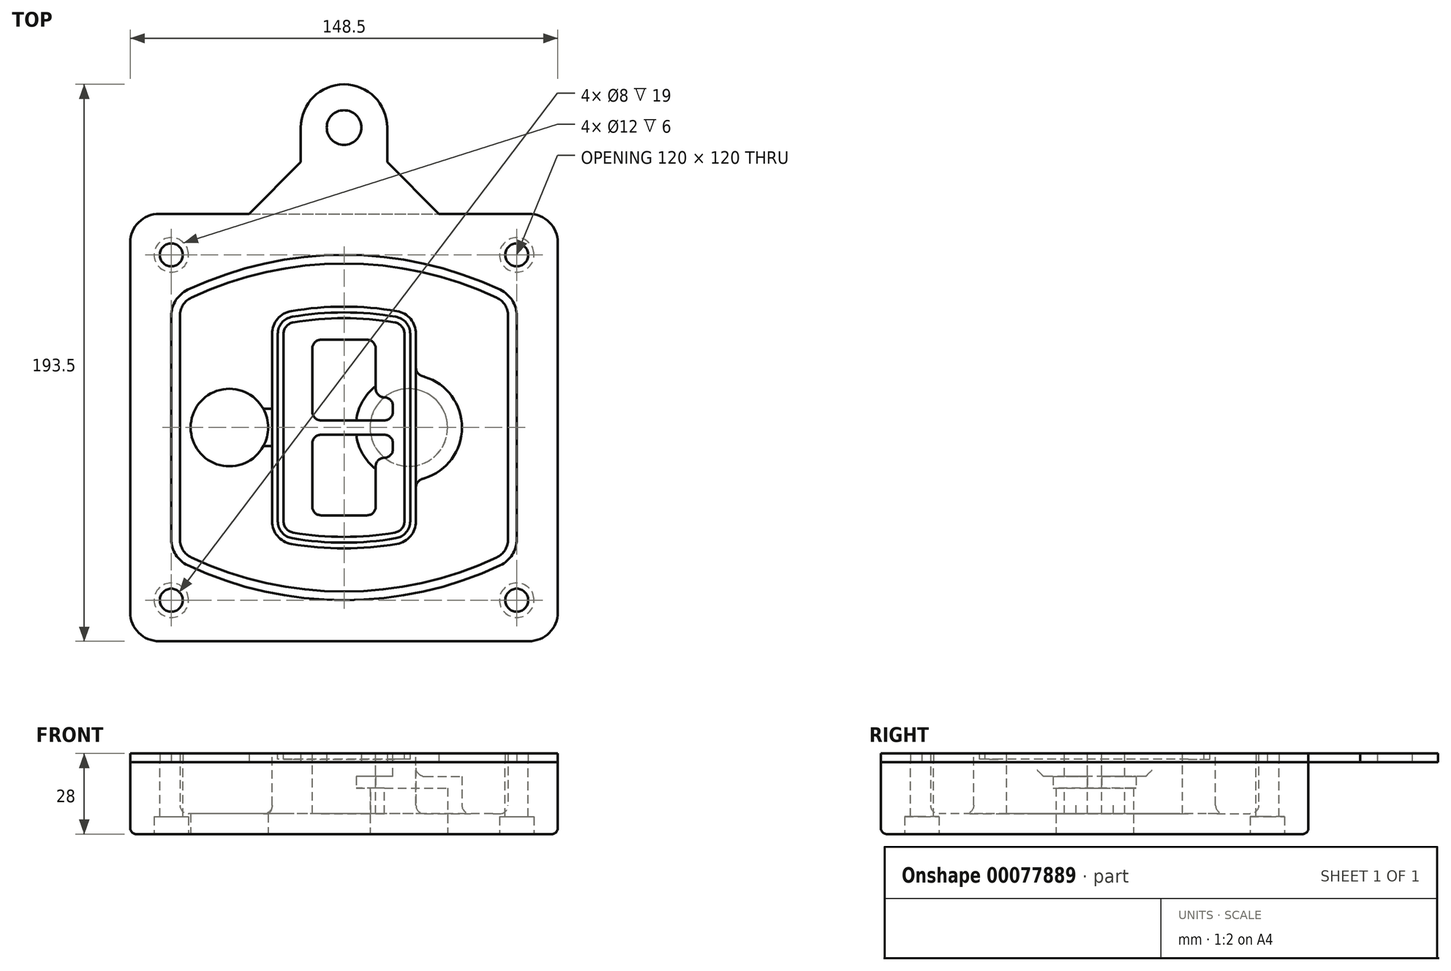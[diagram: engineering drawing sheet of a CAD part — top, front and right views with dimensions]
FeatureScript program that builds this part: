
annotation { "Feature Type Name" : "Feature", "Feature Type Description" : "" }
export const myFeature = defineFeature(function(context is Context, id is Id, definition is map)
    precondition{}
    {
        {
            var Q0;
            Q0=qCreatedBy(makeId("Top.planeOp"),FACE);
            var sketch = newSketch(context, id + "F0", { "sketchPlane" : qUnion([Q0])});
            skPoint(sketch, "E0.rect.middle", {"position": v(0, 0) * mm});
            skLineSegment(sketch, "E1.bottom", {"start": v(-64.25, -74.25) * mm, "end": v(64.25, -74.25) * mm});
            skLineSegment(sketch, "E1.top", {"start": v(-64.25, 74.25) * mm, "end": v(64.25, 74.25) * mm});
            skLineSegment(sketch, "E1.left", {"start": v(-74.25, -64.25) * mm, "end": v(-74.25, 64.25) * mm});
            skLineSegment(sketch, "E1.right", {"start": v(74.25, -64.25) * mm, "end": v(74.25, 64.25) * mm});
            skLineSegment(sketch, "E2", {"start": v(-74.25, 74.25) * mm, "end": v(74.25, -74.25) * mm, "construction": true});
            skLineSegment(sketch, "E3", {"start": v(74.25, 74.25) * mm, "end": v(-74.25, -74.25) * mm, "construction": true});
            skCircle(sketch, "E4", {"center": v(-60, 60) * mm, "radius": 4 * mm});
            skCircle(sketch, "E5", {"center": v(60, 60) * mm, "radius": 4 * mm});
            skCircle(sketch, "E6", {"center": v(60, -60) * mm, "radius": 4 * mm});
            skCircle(sketch, "E7", {"center": v(-60, -60) * mm, "radius": 4 * mm});
            skLineSegment(sketch, "E8", {"start": v(-60, 60) * mm, "end": v(60, 60) * mm, "construction": true});
            skLineSegment(sketch, "E9", {"start": v(60, 60) * mm, "end": v(60, -60) * mm, "construction": true});
            skLineSegment(sketch, "E10", {"start": v(60, -60) * mm, "end": v(-60, -60) * mm, "construction": true});
            skLineSegment(sketch, "E11", {"start": v(-60, -60) * mm, "end": v(-60, 60) * mm, "construction": true});
            skLineSegment(sketch, "E12", {"start": v(-60, 38.83) * mm, "end": v(-60, -38.83) * mm});
            skLineSegment(sketch, "E13", {"start": v(60, 38.83) * mm, "end": v(60, -38.83) * mm});
            skArc(sketch, "E14", {"start": v(54.26, 47.88) * mm, "mid": v(0, 60) * mm, "end": v(-54.26, 47.88) * mm});
            skArc(sketch, "E15", {"start": v(-54.26, -47.88) * mm, "mid": v(0, -60) * mm, "end": v(54.26, -47.88) * mm});
            skLineSegment(sketch, "E16", {"start": v(-60, 0) * mm, "end": v(60, 0) * mm, "construction": true});
            skPoint(sketch, "E17.visualSharp", {"position": v(-60, -45) * mm});
            skArc(sketch, "E17.filletArc", {"start": v(-60, -38.83) * mm, "mid": v(-58.44, -44.2) * mm, "end": v(-54.26, -47.88) * mm});
            skPoint(sketch, "E18.visualSharp", {"position": v(-60, 45) * mm});
            skArc(sketch, "E18.filletArc", {"start": v(-54.26, 47.88) * mm, "mid": v(-58.44, 44.2) * mm, "end": v(-60, 38.83) * mm});
            skPoint(sketch, "E19.visualSharp", {"position": v(60, 45) * mm});
            skArc(sketch, "E19.filletArc", {"start": v(60, 38.83) * mm, "mid": v(58.44, 44.2) * mm, "end": v(54.26, 47.88) * mm});
            skPoint(sketch, "E20.visualSharp", {"position": v(60, -45) * mm});
            skArc(sketch, "E20.filletArc", {"start": v(54.26, -47.88) * mm, "mid": v(58.44, -44.2) * mm, "end": v(60, -38.83) * mm});
            skPoint(sketch, "E21.visualSharp", {"position": v(-74.25, 74.25) * mm});
            skArc(sketch, "E21.filletArc", {"start": v(-64.25, 74.25) * mm, "mid": v(-71.32, 71.32) * mm, "end": v(-74.25, 64.25) * mm});
            skPoint(sketch, "E22.visualSharp", {"position": v(74.25, 74.25) * mm});
            skArc(sketch, "E22.filletArc", {"start": v(74.25, 64.25) * mm, "mid": v(71.32, 71.32) * mm, "end": v(64.25, 74.25) * mm});
            skPoint(sketch, "E23.visualSharp", {"position": v(74.25, -74.25) * mm});
            skArc(sketch, "E23.filletArc", {"start": v(64.25, -74.25) * mm, "mid": v(71.32, -71.32) * mm, "end": v(74.25, -64.25) * mm});
            skPoint(sketch, "E24.visualSharp", {"position": v(-74.25, -74.25) * mm});
            skArc(sketch, "E24.filletArc", {"start": v(-74.25, -64.25) * mm, "mid": v(-71.32, -71.32) * mm, "end": v(-64.25, -74.25) * mm});
            skArc(sketch, "E25.0", {"start": v(57, 38.83) * mm, "mid": v(55.9, 42.58) * mm, "end": v(52.98, 45.17) * mm});
            skLineSegment(sketch, "E25.1", {"start": v(57, 38.83) * mm, "end": v(57, -38.83) * mm});
            skArc(sketch, "E25.2", {"start": v(52.98, -45.17) * mm, "mid": v(55.9, -42.58) * mm, "end": v(57, -38.83) * mm});
            skArc(sketch, "E25.3", {"start": v(-52.98, -45.17) * mm, "mid": v(0, -57) * mm, "end": v(52.98, -45.17) * mm});
            skArc(sketch, "E25.4", {"start": v(-57, -38.83) * mm, "mid": v(-55.9, -42.58) * mm, "end": v(-52.98, -45.17) * mm});
            skArc(sketch, "E25.5", {"start": v(52.98, 45.17) * mm, "mid": v(0, 57) * mm, "end": v(-52.98, 45.17) * mm});
            skLineSegment(sketch, "E25.6", {"start": v(-57, 38.83) * mm, "end": v(-57, -38.83) * mm});
            skArc(sketch, "E25.7", {"start": v(-52.98, 45.17) * mm, "mid": v(-55.9, 42.58) * mm, "end": v(-57, 38.83) * mm});
            skArc(sketch, "E26.0", {"start": v(-55.96, 51.5) * mm, "mid": v(-61.82, 46.33) * mm, "end": v(-64, 38.83) * mm});
            skArc(sketch, "E26.1", {"start": v(55.96, 51.5) * mm, "mid": v(0, 64) * mm, "end": v(-55.96, 51.5) * mm});
            skArc(sketch, "E26.2", {"start": v(64, 38.83) * mm, "mid": v(61.82, 46.33) * mm, "end": v(55.96, 51.5) * mm});
            skLineSegment(sketch, "E26.3", {"start": v(64, 38.83) * mm, "end": v(64, -38.83) * mm});
            skArc(sketch, "E26.4", {"start": v(55.96, -51.5) * mm, "mid": v(61.82, -46.33) * mm, "end": v(64, -38.83) * mm});
            skLineSegment(sketch, "E26.5", {"start": v(-64, 38.83) * mm, "end": v(-64, -38.83) * mm});
            skArc(sketch, "E26.6", {"start": v(-55.96, -51.5) * mm, "mid": v(0, -64) * mm, "end": v(55.96, -51.5) * mm});
            skArc(sketch, "E26.7", {"start": v(-64, -38.83) * mm, "mid": v(-61.82, -46.33) * mm, "end": v(-55.96, -51.5) * mm});
            skSolve(sketch);
        }
        {
            var Q0;
            Q0=makeQuery(id+"F0.imprint","IMPRINT",FACE,{"disambiguationData":[TD([[makeQuery(id+"F0.imprint","IMPRINT",EDGE,{"derivedFrom":sQuery(id+"F0.wireOp",EDGE,"E1.bottom")}),1.0]])]});
            var Q1;
            Q1=makeQuery(id+"F0.imprint","IMPRINT",FACE,{"disambiguationData":[TD([[makeQuery(id+"F0.imprint","IMPRINT",EDGE,{"derivedFrom":sQuery(id+"F0.wireOp",EDGE,"E12")}),1.0]])]});
            var Q2;
            Q2=makeQuery(id+"F0.imprint","IMPRINT",FACE,{"disambiguationData":[TD([[makeQuery(id+"F0.imprint","IMPRINT",EDGE,{"derivedFrom":sQuery(id+"F0.wireOp",EDGE,"E25.0")}),1.0]])]});
            var Q3;
            Q3=makeQuery(id+"F0.imprint","IMPRINT",FACE,{"disambiguationData":[TD([[makeQuery(id+"F0.imprint","IMPRINT",EDGE,{"derivedFrom":sQuery(id+"F0.wireOp",EDGE,"E12")}),-1.0]])]});
            extrude(context, id + "F1", {"entities" : qUnion([Q0, Q1, Q2, Q3]), "oppositeDirection" : true, "depth" : 25 * mm});
        }
        {
            var Q0;
            Q0=makeQuery(id+"F0.imprint","IMPRINT",FACE,{"disambiguationData":[TD([[makeQuery(id+"F0.imprint","IMPRINT",EDGE,{"derivedFrom":sQuery(id+"F0.wireOp",EDGE,"E12")}),1.0]])]});
            extrude(context, id + "F2", {"entities" : qUnion([Q0]), "operationType" : NewBodyOperationType.ADD, "depth" : 3 * mm});
        }
        {
            var Q0;
            Q0=makeQuery(id+"F0.imprint","IMPRINT",FACE,{"disambiguationData":[TD([[makeQuery(id+"F0.imprint","IMPRINT",EDGE,{"derivedFrom":sQuery(id+"F0.wireOp",EDGE,"E25.0")}),1.0]])]});
            extrude(context, id + "F3", {"entities" : qUnion([Q0]), "operationType" : NewBodyOperationType.REMOVE, "oppositeDirection" : true, "depth" : 18 * mm});
        }
        {
            var Q0;
            Q0=makeQuery(id+"F2.opExtrude","CAP_FACE",FACE,{"disambiguationData":[OSD([sQuery(id+"F0.wireOp",EDGE,"E12"),sQuery(id+"F0.wireOp",EDGE,"E13"),sQuery(id+"F0.wireOp",EDGE,"E14"),sQuery(id+"F0.wireOp",EDGE,"E15"),sQuery(id+"F0.wireOp",EDGE,"E17.filletArc"),sQuery(id+"F0.wireOp",EDGE,"E18.filletArc"),sQuery(id+"F0.wireOp",EDGE,"E19.filletArc"),sQuery(id+"F0.wireOp",EDGE,"E20.filletArc"),sQuery(id+"F0.wireOp",EDGE,"E25.0"),sQuery(id+"F0.wireOp",EDGE,"E25.1"),sQuery(id+"F0.wireOp",EDGE,"E25.2"),sQuery(id+"F0.wireOp",EDGE,"E25.3"),sQuery(id+"F0.wireOp",EDGE,"E25.4"),sQuery(id+"F0.wireOp",EDGE,"E25.5"),sQuery(id+"F0.wireOp",EDGE,"E25.6"),sQuery(id+"F0.wireOp",EDGE,"E25.7")])],"isStart":false});
            var sketch = newSketch(context, id + "F4", { "sketchPlane" : qUnion([Q0])});
            skArc(sketch, "E27.0", {"start": v(-18.34, -40.45) * mm, "mid": v(0, -42) * mm, "end": v(18.34, -40.45) * mm});
            skArc(sketch, "E28.0", {"start": v(18.34, 40.45) * mm, "mid": v(0, 42) * mm, "end": v(-18.34, 40.45) * mm});
            skLineSegment(sketch, "E29", {"start": v(-25, 32.57) * mm, "end": v(-25, -32.57) * mm});
            skLineSegment(sketch, "E30", {"start": v(25, 32.57) * mm, "end": v(25, -32.57) * mm});
            skLineSegment(sketch, "E31", {"start": v(-25, 39.1) * mm, "end": v(25, 39.1) * mm, "construction": true});
            skLineSegment(sketch, "E32", {"start": v(-25, -39.1) * mm, "end": v(25, -39.1) * mm, "construction": true});
            skPoint(sketch, "E33.visualSharp", {"position": v(-25, 39.1) * mm});
            skArc(sketch, "E33.filletArc", {"start": v(-18.34, 40.45) * mm, "mid": v(-23.11, 37.73) * mm, "end": v(-25, 32.57) * mm});
            skPoint(sketch, "E34.visualSharp", {"position": v(25, 39.1) * mm});
            skArc(sketch, "E34.filletArc", {"start": v(25, 32.57) * mm, "mid": v(23.11, 37.73) * mm, "end": v(18.34, 40.45) * mm});
            skPoint(sketch, "E35.visualSharp", {"position": v(25, -39.1) * mm});
            skArc(sketch, "E35.filletArc", {"start": v(18.34, -40.45) * mm, "mid": v(23.11, -37.73) * mm, "end": v(25, -32.57) * mm});
            skPoint(sketch, "E36.visualSharp", {"position": v(-25, -39.1) * mm});
            skArc(sketch, "E36.filletArc", {"start": v(-25, -32.57) * mm, "mid": v(-23.11, -37.73) * mm, "end": v(-18.34, -40.45) * mm});
            skArc(sketch, "E37.0", {"start": v(52.98, 45.17) * mm, "mid": v(0, 57) * mm, "end": v(-52.98, 45.17) * mm});
            skArc(sketch, "E37.1", {"start": v(-52.98, 45.17) * mm, "mid": v(-55.9, 42.58) * mm, "end": v(-57, 38.83) * mm});
            skLineSegment(sketch, "E37.2", {"start": v(-57, 38.83) * mm, "end": v(-57, -38.83) * mm});
            skArc(sketch, "E37.3", {"start": v(-57, -38.83) * mm, "mid": v(-55.9, -42.58) * mm, "end": v(-52.98, -45.17) * mm});
            skArc(sketch, "E37.4", {"start": v(-52.98, -45.17) * mm, "mid": v(0, -57) * mm, "end": v(52.98, -45.17) * mm});
            skArc(sketch, "E37.5", {"start": v(52.98, -45.17) * mm, "mid": v(55.9, -42.58) * mm, "end": v(57, -38.83) * mm});
            skLineSegment(sketch, "E37.6", {"start": v(57, 38.83) * mm, "end": v(57, -38.83) * mm});
            skArc(sketch, "E37.7", {"start": v(57, 38.83) * mm, "mid": v(55.9, 42.58) * mm, "end": v(52.98, 45.17) * mm});
            skLineSegment(sketch, "E38.0", {"start": v(23, 32.57) * mm, "end": v(23, -32.57) * mm});
            skArc(sketch, "E38.1", {"start": v(18, -38.48) * mm, "mid": v(21.58, -36.44) * mm, "end": v(23, -32.57) * mm});
            skArc(sketch, "E38.2", {"start": v(-18, -38.48) * mm, "mid": v(0, -40) * mm, "end": v(18, -38.48) * mm});
            skArc(sketch, "E38.3", {"start": v(-23, -32.57) * mm, "mid": v(-21.58, -36.44) * mm, "end": v(-18, -38.48) * mm});
            skLineSegment(sketch, "E38.4", {"start": v(-23, 32.57) * mm, "end": v(-23, -32.57) * mm});
            skArc(sketch, "E38.5", {"start": v(23, 32.57) * mm, "mid": v(21.58, 36.44) * mm, "end": v(18, 38.48) * mm});
            skArc(sketch, "E38.6", {"start": v(-18, 38.48) * mm, "mid": v(-21.58, 36.44) * mm, "end": v(-23, 32.57) * mm});
            skArc(sketch, "E38.7", {"start": v(18, 38.48) * mm, "mid": v(0, 40) * mm, "end": v(-18, 38.48) * mm});
            skArc(sketch, "E39.0", {"start": v(21, 32.57) * mm, "mid": v(20.06, 35.15) * mm, "end": v(17.67, 36.5) * mm});
            skLineSegment(sketch, "E39.1", {"start": v(21, 32.57) * mm, "end": v(21, -32.57) * mm});
            skArc(sketch, "E39.2", {"start": v(17.67, -36.5) * mm, "mid": v(20.06, -35.15) * mm, "end": v(21, -32.57) * mm});
            skArc(sketch, "E39.3", {"start": v(-17.67, -36.5) * mm, "mid": v(0, -38) * mm, "end": v(17.67, -36.5) * mm});
            skArc(sketch, "E39.4", {"start": v(-21, -32.57) * mm, "mid": v(-20.06, -35.15) * mm, "end": v(-17.67, -36.5) * mm});
            skArc(sketch, "E39.5", {"start": v(17.67, 36.5) * mm, "mid": v(0, 38) * mm, "end": v(-17.67, 36.5) * mm});
            skLineSegment(sketch, "E39.6", {"start": v(-21, 32.57) * mm, "end": v(-21, -32.57) * mm});
            skArc(sketch, "E39.7", {"start": v(-17.67, 36.5) * mm, "mid": v(-20.06, 35.15) * mm, "end": v(-21, 32.57) * mm});
            skLineSegment(sketch, "E40", {"start": v(-25, 0) * mm, "end": v(25, 0) * mm, "construction": true});
            skLineSegment(sketch, "E41", {"start": v(-11, 5.5) * mm, "end": v(-11, 27.5) * mm});
            skLineSegment(sketch, "E42", {"start": v(-8, 30.5) * mm, "end": v(8, 30.5) * mm});
            skLineSegment(sketch, "E43", {"start": v(11, 27.5) * mm, "end": v(11, 13.5) * mm});
            skLineSegment(sketch, "E44", {"start": v(14, 10.5) * mm, "end": v(14, 10.5) * mm});
            skLineSegment(sketch, "E45", {"start": v(17, 7.5) * mm, "end": v(17, 5.5) * mm});
            skLineSegment(sketch, "E46", {"start": v(14, 2.5) * mm, "end": v(-8, 2.5) * mm});
            skPoint(sketch, "E47.visualSharp", {"position": v(-11, 30.5) * mm});
            skArc(sketch, "E47.filletArc", {"start": v(-8, 30.5) * mm, "mid": v(-10.12, 29.62) * mm, "end": v(-11, 27.5) * mm});
            skPoint(sketch, "E48.visualSharp", {"position": v(11, 30.5) * mm});
            skArc(sketch, "E48.filletArc", {"start": v(11, 27.5) * mm, "mid": v(10.12, 29.62) * mm, "end": v(8, 30.5) * mm});
            skPoint(sketch, "E49.visualSharp", {"position": v(11, 10.5) * mm});
            skArc(sketch, "E49.filletArc", {"start": v(11, 13.5) * mm, "mid": v(11.88, 11.38) * mm, "end": v(14, 10.5) * mm});
            skPoint(sketch, "E50.visualSharp", {"position": v(17, 10.5) * mm});
            skArc(sketch, "E50.filletArc", {"start": v(17, 7.5) * mm, "mid": v(16.12, 9.62) * mm, "end": v(14, 10.5) * mm});
            skPoint(sketch, "E51.visualSharp", {"position": v(17, 2.5) * mm});
            skArc(sketch, "E51.filletArc", {"start": v(14, 2.5) * mm, "mid": v(16.12, 3.38) * mm, "end": v(17, 5.5) * mm});
            skPoint(sketch, "E52.visualSharp", {"position": v(-11, 2.5) * mm});
            skArc(sketch, "E52.filletArc", {"start": v(-11, 5.5) * mm, "mid": v(-10.12, 3.38) * mm, "end": v(-8, 2.5) * mm});
            skLineSegment(sketch, "E53.0.MirrorCS", {"start": v(14, -2.5) * mm, "end": v(-8, -2.5) * mm});
            skArc(sketch, "E54.0.MirrorCS", {"start": v(-11, -5.5) * mm, "mid": v(-10.12, -3.38) * mm, "end": v(-8, -2.5) * mm});
            skLineSegment(sketch, "E55.0.MirrorCS", {"start": v(-11, -5.5) * mm, "end": v(-11, -27.5) * mm});
            skArc(sketch, "E56.0.MirrorCS", {"start": v(-8, -30.5) * mm, "mid": v(-10.12, -29.62) * mm, "end": v(-11, -27.5) * mm});
            skLineSegment(sketch, "E57.0.MirrorCS", {"start": v(-8, -30.5) * mm, "end": v(8, -30.5) * mm});
            skArc(sketch, "E58.0.MirrorCS", {"start": v(11, -27.5) * mm, "mid": v(10.12, -29.62) * mm, "end": v(8, -30.5) * mm});
            skLineSegment(sketch, "E59.0.MirrorCS", {"start": v(11, -27.5) * mm, "end": v(11, -13.5) * mm});
            skArc(sketch, "E60.0.MirrorCS", {"start": v(11, -13.5) * mm, "mid": v(11.88, -11.38) * mm, "end": v(14, -10.5) * mm});
            skArc(sketch, "E61.0.MirrorCS", {"start": v(17, -7.5) * mm, "mid": v(16.12, -9.62) * mm, "end": v(14, -10.5) * mm});
            skLineSegment(sketch, "E62.0.MirrorCS", {"start": v(17, -7.5) * mm, "end": v(17, -5.5) * mm});
            skArc(sketch, "E63.0.MirrorCS", {"start": v(14, -2.5) * mm, "mid": v(16.12, -3.38) * mm, "end": v(17, -5.5) * mm});
            skSolve(sketch);
        }
        {
            var Q0;
            Q0=makeQuery(id+"F4.imprint","IMPRINT",FACE,{"disambiguationData":[TD([[makeQuery(id+"F4.imprint","IMPRINT",EDGE,{"derivedFrom":sQuery(id+"F4.wireOp",EDGE,"E27.0")}),1.0]])]});
            var Q1;
            Q1=makeQuery(id+"F4.imprint","IMPRINT",FACE,{"disambiguationData":[TD([[makeQuery(id+"F4.imprint","IMPRINT",EDGE,{"derivedFrom":sQuery(id+"F4.wireOp",EDGE,"E38.0")}),-1.0]])]});
            var Q2;
            Q2=makeQuery(id+"F4.imprint","IMPRINT",FACE,{"disambiguationData":[TD([[makeQuery(id+"F4.imprint","IMPRINT",EDGE,{"derivedFrom":sQuery(id+"F4.wireOp",EDGE,"E39.0")}),1.0]])]});
            extrude(context, id + "F5", {"entities" : qUnion([Q0, Q1, Q2]), "operationType" : NewBodyOperationType.ADD, "endBound" : BoundingType.UP_TO_NEXT, "oppositeDirection" : true, "depth" : 25 * mm});
        }
        {
            var Q0;
            Q0=makeQuery(id+"F4.imprint","IMPRINT",FACE,{"disambiguationData":[TD([[makeQuery(id+"F4.imprint","IMPRINT",EDGE,{"derivedFrom":sQuery(id+"F4.wireOp",EDGE,"E38.0")}),-1.0]])]});
            extrude(context, id + "F6", {"entities" : qUnion([Q0]), "operationType" : NewBodyOperationType.REMOVE, "oppositeDirection" : true, "depth" : 2 * mm});
        }
        {
            var Q0;
            Q0=makeQuery(id+"F1.opExtrude","CAP_FACE",FACE,{"disambiguationData":[OSD([sQuery(id+"F0.wireOp",EDGE,"E1.bottom"),sQuery(id+"F0.wireOp",EDGE,"E1.top"),sQuery(id+"F0.wireOp",EDGE,"E1.left"),sQuery(id+"F0.wireOp",EDGE,"E1.right"),sQuery(id+"F0.wireOp",EDGE,"E4"),sQuery(id+"F0.wireOp",EDGE,"E5"),sQuery(id+"F0.wireOp",EDGE,"E6"),sQuery(id+"F0.wireOp",EDGE,"E7"),sQuery(id+"F0.wireOp",EDGE,"E21.filletArc"),sQuery(id+"F0.wireOp",EDGE,"E22.filletArc"),sQuery(id+"F0.wireOp",EDGE,"E23.filletArc"),sQuery(id+"F0.wireOp",EDGE,"E24.filletArc")])],"isStart":false});
            var sketch = newSketch(context, id + "F7", { "sketchPlane" : qUnion([Q0])});
            skCircle(sketch, "E64", {"center": v(22.5, 0) * mm, "radius": 13.47 * mm});
            skCircle(sketch, "E65", {"center": v(-39.81, 0) * mm, "radius": 13.47 * mm});
            skLineSegment(sketch, "E66", {"start": v(74.25, 0) * mm, "end": v(-74.25, 0) * mm});
            skCircle(sketch, "E67", {"center": v(22.5, 0) * mm, "radius": 18.47 * mm});
            skCircle(sketch, "E68", {"center": v(60, -60) * mm, "radius": 6 * mm});
            skCircle(sketch, "E69", {"center": v(-60, -60) * mm, "radius": 6 * mm});
            skCircle(sketch, "E70", {"center": v(-60, 60) * mm, "radius": 6 * mm});
            skCircle(sketch, "E71", {"center": v(60, 60) * mm, "radius": 6 * mm});
            skSolve(sketch);
        }
        {
            var Q0;
            {var subQ1=sQuery(id+"F7.wireOp",EDGE,"E66");var subQ4=sQuery(id+"F7.wireOp",EDGE,"E64");var subQ6=makeQuery(id+"F7.imprint","INTERSECT",VERTEX,{"disambiguationData":[OD(0.0)],"derivedFrom":[subQ4,subQ1]});Q0=makeQuery(id+"F7.imprint","IMPRINT",FACE,{"disambiguationData":[TD([[makeQuery(id+"F7.imprint","IMPRINT",EDGE,{"disambiguationData":[TD([[subQ6,-1.0]])],"derivedFrom":subQ4}),-1.0]])]});}
            var Q1;
            {var subQ0=sQuery(id+"F7.wireOp",EDGE,"E66");var subQ1=sQuery(id+"F7.wireOp",EDGE,"E64");var subQ3=makeQuery(id+"F7.imprint","INTERSECT",VERTEX,{"disambiguationData":[OD(0.0)],"derivedFrom":[subQ1,subQ0]});Q1=makeQuery(id+"F7.imprint","IMPRINT",FACE,{"disambiguationData":[TD([[makeQuery(id+"F7.imprint","IMPRINT",EDGE,{"disambiguationData":[TD([[subQ3,-1.0]])],"derivedFrom":subQ1}),1.0]])]});}
            var Q2;
            {var subQ0=sQuery(id+"F7.wireOp",EDGE,"E66");var subQ1=sQuery(id+"F7.wireOp",EDGE,"E64");var subQ3=makeQuery(id+"F7.imprint","INTERSECT",VERTEX,{"disambiguationData":[OD(0.0)],"derivedFrom":[subQ1,subQ0]});Q2=makeQuery(id+"F7.imprint","IMPRINT",FACE,{"disambiguationData":[TD([[makeQuery(id+"F7.imprint","IMPRINT",EDGE,{"disambiguationData":[TD([[subQ3,1.0]])],"derivedFrom":subQ1}),1.0]])]});}
            var Q3;
            {var subQ1=sQuery(id+"F7.wireOp",EDGE,"E66");var subQ4=sQuery(id+"F7.wireOp",EDGE,"E64");var subQ6=makeQuery(id+"F7.imprint","INTERSECT",VERTEX,{"disambiguationData":[OD(0.0)],"derivedFrom":[subQ4,subQ1]});Q3=makeQuery(id+"F7.imprint","IMPRINT",FACE,{"disambiguationData":[TD([[makeQuery(id+"F7.imprint","IMPRINT",EDGE,{"disambiguationData":[TD([[subQ6,1.0]])],"derivedFrom":subQ4}),-1.0]])]});}
            extrude(context, id + "F8", {"entities" : qUnion([Q0, Q1, Q2, Q3]), "operationType" : NewBodyOperationType.ADD, "oppositeDirection" : true, "depth" : 20 * mm});
        }
        {
            var Q0;
            {var subQ0=sQuery(id+"F7.wireOp",EDGE,"E66");var subQ1=sQuery(id+"F7.wireOp",EDGE,"E64");var subQ3=makeQuery(id+"F7.imprint","INTERSECT",VERTEX,{"disambiguationData":[OD(0.0)],"derivedFrom":[subQ1,subQ0]});Q0=makeQuery(id+"F7.imprint","IMPRINT",FACE,{"disambiguationData":[TD([[makeQuery(id+"F7.imprint","IMPRINT",EDGE,{"disambiguationData":[TD([[subQ3,-1.0]])],"derivedFrom":subQ1}),1.0]])]});}
            var Q1;
            {var subQ0=sQuery(id+"F7.wireOp",EDGE,"E66");var subQ1=sQuery(id+"F7.wireOp",EDGE,"E64");var subQ3=makeQuery(id+"F7.imprint","INTERSECT",VERTEX,{"disambiguationData":[OD(0.0)],"derivedFrom":[subQ1,subQ0]});Q1=makeQuery(id+"F7.imprint","IMPRINT",FACE,{"disambiguationData":[TD([[makeQuery(id+"F7.imprint","IMPRINT",EDGE,{"disambiguationData":[TD([[subQ3,1.0]])],"derivedFrom":subQ1}),1.0]])]});}
            extrude(context, id + "F9", {"entities" : qUnion([Q0, Q1]), "operationType" : NewBodyOperationType.REMOVE, "oppositeDirection" : true, "depth" : 16 * mm});
        }
        {
            var Q0;
            {var subQ0=sQuery(id+"F7.wireOp",EDGE,"E66");var subQ1=sQuery(id+"F7.wireOp",EDGE,"E65");var subQ3=makeQuery(id+"F7.imprint","INTERSECT",VERTEX,{"disambiguationData":[OD(0.0)],"derivedFrom":[subQ1,subQ0]});Q0=makeQuery(id+"F7.imprint","IMPRINT",FACE,{"disambiguationData":[TD([[makeQuery(id+"F7.imprint","IMPRINT",EDGE,{"disambiguationData":[TD([[subQ3,-1.0]])],"derivedFrom":subQ1}),1.0]])]});}
            var Q1;
            {var subQ0=sQuery(id+"F7.wireOp",EDGE,"E66");var subQ1=sQuery(id+"F7.wireOp",EDGE,"E65");var subQ3=makeQuery(id+"F7.imprint","INTERSECT",VERTEX,{"disambiguationData":[OD(0.0)],"derivedFrom":[subQ1,subQ0]});Q1=makeQuery(id+"F7.imprint","IMPRINT",FACE,{"disambiguationData":[TD([[makeQuery(id+"F7.imprint","IMPRINT",EDGE,{"disambiguationData":[TD([[subQ3,1.0]])],"derivedFrom":subQ1}),1.0]])]});}
            extrude(context, id + "F10", {"entities" : qUnion([Q0, Q1]), "operationType" : NewBodyOperationType.REMOVE, "oppositeDirection" : true, "depth" : 25 * mm});
        }
        {
            var Q0;
            Q0=makeQuery(id+"F7.imprint","IMPRINT",FACE,{"disambiguationData":[TD([[makeQuery(id+"F7.imprint","IMPRINT",EDGE,{"derivedFrom":sQuery(id+"F7.wireOp",EDGE,"E68")}),1.0]])]});
            var Q1;
            Q1=makeQuery(id+"F7.imprint","IMPRINT",FACE,{"disambiguationData":[TD([[makeQuery(id+"F7.imprint","IMPRINT",EDGE,{"derivedFrom":makeQuery(id+"F1.opExtrude","CAP_EDGE",EDGE,{"disambiguationData":[OSD([sQuery(id+"F0.wireOp",EDGE,"E5")])],"isStart":false})}),-1.0]])]});
            var Q2;
            Q2=makeQuery(id+"F7.imprint","IMPRINT",FACE,{"disambiguationData":[TD([[makeQuery(id+"F7.imprint","IMPRINT",EDGE,{"derivedFrom":sQuery(id+"F7.wireOp",EDGE,"E69")}),1.0]])]});
            var Q3;
            Q3=makeQuery(id+"F7.imprint","IMPRINT",FACE,{"disambiguationData":[TD([[makeQuery(id+"F7.imprint","IMPRINT",EDGE,{"derivedFrom":makeQuery(id+"F1.opExtrude","CAP_EDGE",EDGE,{"disambiguationData":[OSD([sQuery(id+"F0.wireOp",EDGE,"E4")])],"isStart":false})}),-1.0]])]});
            var Q4;
            Q4=makeQuery(id+"F7.imprint","IMPRINT",FACE,{"disambiguationData":[TD([[makeQuery(id+"F7.imprint","IMPRINT",EDGE,{"derivedFrom":sQuery(id+"F7.wireOp",EDGE,"E70")}),1.0]])]});
            var Q5;
            Q5=makeQuery(id+"F7.imprint","IMPRINT",FACE,{"disambiguationData":[TD([[makeQuery(id+"F7.imprint","IMPRINT",EDGE,{"derivedFrom":makeQuery(id+"F1.opExtrude","CAP_EDGE",EDGE,{"disambiguationData":[OSD([sQuery(id+"F0.wireOp",EDGE,"E7")])],"isStart":false})}),-1.0]])]});
            var Q6;
            Q6=makeQuery(id+"F7.imprint","IMPRINT",FACE,{"disambiguationData":[TD([[makeQuery(id+"F7.imprint","IMPRINT",EDGE,{"derivedFrom":sQuery(id+"F7.wireOp",EDGE,"E71")}),1.0]])]});
            var Q7;
            Q7=makeQuery(id+"F7.imprint","IMPRINT",FACE,{"disambiguationData":[TD([[makeQuery(id+"F7.imprint","IMPRINT",EDGE,{"derivedFrom":makeQuery(id+"F1.opExtrude","CAP_EDGE",EDGE,{"disambiguationData":[OSD([sQuery(id+"F0.wireOp",EDGE,"E6")])],"isStart":false})}),-1.0]])]});
            extrude(context, id + "F11", {"entities" : qUnion([Q0, Q1, Q2, Q3, Q4, Q5, Q6, Q7]), "operationType" : NewBodyOperationType.REMOVE, "oppositeDirection" : true, "depth" : 6 * mm});
        }
        {
            var Q0;
            Q0=makeQuery(id+"F9.boolean.opBoolean","COPY",FACE,{"derivedFrom":makeQuery(id+"F9.opExtrude","CAP_FACE",FACE,{"disambiguationData":[OSD([sQuery(id+"F7.wireOp",EDGE,"E64")])],"isStart":false})});
            var sketch = newSketch(context, id + "F12", { "sketchPlane" : qUnion([Q0])});
            skArc(sketch, "E72.0", {"start": v(11, 14.45) * mm, "mid": v(6.45, 9.13) * mm, "end": v(4.2, 2.5) * mm});
            skArc(sketch, "E72.1", {"start": v(4.2, -2.5) * mm, "mid": v(6.45, -9.13) * mm, "end": v(11, -14.45) * mm});
            skLineSegment(sketch, "E73", {"start": v(4.2, -2.5) * mm, "end": v(14, -2.5) * mm});
            skLineSegment(sketch, "E74.0", {"start": v(14, 2.5) * mm, "end": v(4.2, 2.5) * mm});
            skArc(sketch, "E74.1", {"start": v(14, 2.5) * mm, "mid": v(16.12, 3.38) * mm, "end": v(17, 5.5) * mm});
            skLineSegment(sketch, "E74.2", {"start": v(17, 7.5) * mm, "end": v(17, 5.5) * mm});
            skArc(sketch, "E74.3", {"start": v(17, 7.5) * mm, "mid": v(16.12, 9.62) * mm, "end": v(14, 10.5) * mm});
            skArc(sketch, "E74.4", {"start": v(11, 13.5) * mm, "mid": v(11.88, 11.38) * mm, "end": v(14, 10.5) * mm});
            skLineSegment(sketch, "E74.5", {"start": v(11, 14.45) * mm, "end": v(11, 13.5) * mm});
            skLineSegment(sketch, "E74.7", {"start": v(14, -2.5) * mm, "end": v(4.2, -2.5) * mm});
            skArc(sketch, "E74.8", {"start": v(14, -2.5) * mm, "mid": v(16.12, -3.38) * mm, "end": v(17, -5.5) * mm});
            skLineSegment(sketch, "E74.9", {"start": v(17, -7.5) * mm, "end": v(17, -5.5) * mm});
            skArc(sketch, "E74.10", {"start": v(17, -7.5) * mm, "mid": v(16.12, -9.62) * mm, "end": v(14, -10.5) * mm});
            skArc(sketch, "E74.11", {"start": v(11, -13.5) * mm, "mid": v(11.88, -11.38) * mm, "end": v(14, -10.5) * mm});
            skLineSegment(sketch, "E74.12", {"start": v(11, -14.45) * mm, "end": v(11, -13.5) * mm});
            skPoint(sketch, "E75.orphan", {"position": v(11, -27.5) * mm});
            skPoint(sketch, "E76.orphan", {"position": v(-8, -2.5) * mm});
            skPoint(sketch, "E77.orphan", {"position": v(-8, 2.5) * mm});
            skPoint(sketch, "E78.orphan", {"position": v(11, 27.5) * mm});
            skSolve(sketch);
        }
        {
            var Q0;
            {var subQ7=sQuery(id+"F12.wireOp",EDGE,"E72.0");var subQ14=sQuery(id+"F12.wireOp",EDGE,"E72.1");var subQ16=sQuery(id+"F12.wireOp",EDGE,"E74.1");var subQ18=sQuery(id+"F12.wireOp",EDGE,"E74.8");Q0=qUnion([makeQuery(id+"F12.imprint","IMPRINT",FACE,{"disambiguationData":[TD([[makeQuery(id+"F12.imprint","IMPRINT",EDGE,{"derivedFrom":subQ7}),1.0]])]}),makeQuery(id+"F12.imprint","IMPRINT",FACE,{"disambiguationData":[TD([[makeQuery(id+"F12.imprint","IMPRINT",EDGE,{"derivedFrom":subQ14}),1.0]])]}),makeQuery(id+"F12.imprint","IMPRINT",FACE,{"disambiguationData":[TD([[makeQuery(id+"F12.imprint","IMPRINT",EDGE,{"derivedFrom":subQ16}),1.0]])]}),makeQuery(id+"F12.imprint","IMPRINT",FACE,{"disambiguationData":[TD([[makeQuery(id+"F12.imprint","IMPRINT",EDGE,{"derivedFrom":subQ18}),-1.0]])]})]);}
            var Q1;
            Q1=makeQuery(id+"F5.boolean.opBoolean","SPLIT",FACE,{"disambiguationData":[TD([makeQuery(id+"F5.opExtrude","SWEPT_FACE",FACE,{"disambiguationData":[OSD([sQuery(id+"F4.wireOp",EDGE,"E41")])]})])],"derivedFrom":makeQuery(id+"F3.boolean.opBoolean","COPY",FACE,{"derivedFrom":makeQuery(id+"F3.opExtrude","CAP_FACE",FACE,{"disambiguationData":[OSD([sQuery(id+"F0.wireOp",EDGE,"E25.0"),sQuery(id+"F0.wireOp",EDGE,"E25.1"),sQuery(id+"F0.wireOp",EDGE,"E25.2"),sQuery(id+"F0.wireOp",EDGE,"E25.3"),sQuery(id+"F0.wireOp",EDGE,"E25.4"),sQuery(id+"F0.wireOp",EDGE,"E25.5"),sQuery(id+"F0.wireOp",EDGE,"E25.6"),sQuery(id+"F0.wireOp",EDGE,"E25.7")])],"isStart":false})})});
            extrude(context, id + "F13", {"entities" : qUnion([Q0]), "operationType" : NewBodyOperationType.REMOVE, "endBound" : BoundingType.UP_TO_SURFACE, "endBoundEntityFace" : qUnion([Q1]), "depth" : 25 * mm});
        }
        {
            var Q0;
            Q0=makeQuery(id+"F3.boolean.opBoolean","COPY",EDGE,{"derivedFrom":makeQuery(id+"F3.opExtrude","CAP_EDGE",EDGE,{"disambiguationData":[OSD([sQuery(id+"F0.wireOp",EDGE,"E25.6")])],"isStart":false})});
            var Q1;
            Q1=makeQuery(id+"F8.boolean.opBoolean","INTERSECT",EDGE,{"derivedFrom":[makeQuery(id+"F5.opExtrude","SWEPT_FACE",FACE,{"disambiguationData":[OSD([sQuery(id+"F4.wireOp",EDGE,"E30")])]}),makeQuery(id+"F8.opExtrude","CAP_FACE",FACE,{"disambiguationData":[OSD([sQuery(id+"F7.wireOp",EDGE,"E67")])],"isStart":false})]});
            var Q2;
            Q2=makeQuery(id+"F8.boolean.opBoolean","INTERSECT",EDGE,{"disambiguationData":[OD(1.0)],"derivedFrom":[makeQuery(id+"F5.opExtrude","SWEPT_FACE",FACE,{"disambiguationData":[OSD([sQuery(id+"F4.wireOp",EDGE,"E30")])]}),makeQuery(id+"F8.opExtrude","SWEPT_FACE",FACE,{"disambiguationData":[OSD([sQuery(id+"F7.wireOp",EDGE,"E67")])]})]});
            var Q3;
            {var subQ0=sQuery(id+"F4.wireOp",EDGE,"E30");Q3=makeQuery(id+"F8.boolean.opBoolean","SPLIT",EDGE,{"disambiguationData":[TD([makeQuery(id+"F5.opExtrude","SWEPT_FACE",FACE,{"disambiguationData":[OSD([sQuery(id+"F4.wireOp",EDGE,"E35.filletArc")])]})])],"derivedFrom":makeQuery(id+"F5.opExtrude","CAP_EDGE",EDGE,{"disambiguationData":[OSD([subQ0])],"isStart":false})});}
            var Q4;
            {var subQ0=sQuery(id+"F0.wireOp",EDGE,"E25.7");var subQ1=sQuery(id+"F0.wireOp",EDGE,"E25.1");var subQ2=sQuery(id+"F0.wireOp",EDGE,"E25.6");var subQ3=sQuery(id+"F0.wireOp",EDGE,"E25.5");var subQ4=sQuery(id+"F0.wireOp",EDGE,"E25.4");var subQ5=sQuery(id+"F0.wireOp",EDGE,"E25.0");var subQ6=sQuery(id+"F0.wireOp",EDGE,"E25.2");var subQ7=sQuery(id+"F0.wireOp",EDGE,"E25.3");Q4=makeQuery(id+"F8.boolean.opBoolean","INTERSECT",EDGE,{"derivedFrom":[makeQuery(id+"F5.boolean.opBoolean","SPLIT",FACE,{"disambiguationData":[TD([makeQuery(id+"F2.opExtrude","SWEPT_FACE",FACE,{"disambiguationData":[OSD([subQ5])]})])],"derivedFrom":makeQuery(id+"F3.boolean.opBoolean","COPY",FACE,{"derivedFrom":makeQuery(id+"F3.opExtrude","CAP_FACE",FACE,{"disambiguationData":[OSD([subQ5,subQ1,subQ6,subQ7,subQ4,subQ3,subQ2,subQ0])],"isStart":false})})}),makeQuery(id+"F8.opExtrude","SWEPT_FACE",FACE,{"disambiguationData":[OSD([sQuery(id+"F7.wireOp",EDGE,"E67")])]})]});}
            var Q5;
            Q5=makeQuery(id+"F8.boolean.opBoolean","INTERSECT",EDGE,{"disambiguationData":[OD(0.0)],"derivedFrom":[makeQuery(id+"F5.opExtrude","SWEPT_FACE",FACE,{"disambiguationData":[OSD([sQuery(id+"F4.wireOp",EDGE,"E30")])]}),makeQuery(id+"F8.opExtrude","SWEPT_FACE",FACE,{"disambiguationData":[OSD([sQuery(id+"F7.wireOp",EDGE,"E67")])]})]});
            fillet(context, id + "F14", {"entities" : qUnion([Q0, Q1, Q2, Q3, Q4, Q5]), "radius" : 3 * mm, "tangentPropagation" : true, "allowEdgeOverflow" : false});
        }
        {
            var Q0;
            Q0=makeQuery(id+"F1.opExtrude","CAP_EDGE",EDGE,{"disambiguationData":[OSD([sQuery(id+"F0.wireOp",EDGE,"E1.bottom")])],"isStart":false});
            fillet(context, id + "F15", {"entities" : qUnion([Q0]), "radius" : 2 * mm, "tangentPropagation" : true, "allowEdgeOverflow" : false});
        }
        {
            var Q0;
            {var subQ0=sQuery(id+"F0.wireOp",EDGE,"E22.filletArc");var subQ1=sQuery(id+"F0.wireOp",EDGE,"E7");var subQ2=sQuery(id+"F0.wireOp",EDGE,"E6");var subQ3=sQuery(id+"F0.wireOp",EDGE,"E5");var subQ4=sQuery(id+"F0.wireOp",EDGE,"E4");var subQ5=sQuery(id+"F0.wireOp",EDGE,"E1.bottom");var subQ6=sQuery(id+"F0.wireOp",EDGE,"E21.filletArc");var subQ7=sQuery(id+"F0.wireOp",EDGE,"E1.top");var subQ8=sQuery(id+"F0.wireOp",EDGE,"E1.left");var subQ9=sQuery(id+"F0.wireOp",EDGE,"E1.right");var subQ10=sQuery(id+"F0.wireOp",EDGE,"E23.filletArc");var subQ11=sQuery(id+"F0.wireOp",EDGE,"E24.filletArc");Q0=makeQuery(id+"F2.boolean.opBoolean","SPLIT",FACE,{"disambiguationData":[TD([makeQuery(id+"F1.opExtrude","SWEPT_FACE",FACE,{"disambiguationData":[OSD([subQ5])]})])],"derivedFrom":makeQuery(id+"F1.opExtrude","CAP_FACE",FACE,{"disambiguationData":[OSD([subQ5,subQ7,subQ8,subQ9,subQ4,subQ3,subQ2,subQ1,subQ6,subQ0,subQ10,subQ11])],"isStart":true})});}
            var sketch = newSketch(context, id + "F16", { "sketchPlane" : qUnion([Q0])});
            skLineSegment(sketch, "E79.0", {"start": v(-74.25, -64.25) * mm, "end": v(-74.25, 64.25) * mm});
            skArc(sketch, "E79.1", {"start": v(-64.25, 74.25) * mm, "mid": v(-71.32, 71.32) * mm, "end": v(-74.25, 64.25) * mm});
            skLineSegment(sketch, "E79.2", {"start": v(-64.25, 74.25) * mm, "end": v(64.25, 74.25) * mm});
            skArc(sketch, "E79.3", {"start": v(-74.25, -64.25) * mm, "mid": v(-71.32, -71.32) * mm, "end": v(-64.25, -74.25) * mm});
            skLineSegment(sketch, "E79.4", {"start": v(-64.25, -74.25) * mm, "end": v(64.25, -74.25) * mm});
            skArc(sketch, "E79.5", {"start": v(64.25, -74.25) * mm, "mid": v(71.32, -71.32) * mm, "end": v(74.25, -64.25) * mm});
            skLineSegment(sketch, "E79.6", {"start": v(74.25, -64.25) * mm, "end": v(74.25, 64.25) * mm});
            skArc(sketch, "E79.7", {"start": v(74.25, 64.25) * mm, "mid": v(71.32, 71.32) * mm, "end": v(64.25, 74.25) * mm});
            skCircle(sketch, "E79.8", {"center": v(60, 60) * mm, "radius": 4 * mm});
            skCircle(sketch, "E79.9", {"center": v(60, -60) * mm, "radius": 4 * mm});
            skCircle(sketch, "E79.10", {"center": v(-60, -60) * mm, "radius": 4 * mm});
            skCircle(sketch, "E79.11", {"center": v(-60, 60) * mm, "radius": 4 * mm});
            skArc(sketch, "E79.12", {"start": v(-54.26, -47.88) * mm, "mid": v(0, -60) * mm, "end": v(54.26, -47.88) * mm});
            skArc(sketch, "E79.13", {"start": v(-60, -38.83) * mm, "mid": v(-58.44, -44.2) * mm, "end": v(-54.26, -47.88) * mm});
            skLineSegment(sketch, "E79.14", {"start": v(-60, 38.83) * mm, "end": v(-60, -38.83) * mm});
            skArc(sketch, "E79.15", {"start": v(-54.26, 47.88) * mm, "mid": v(-58.44, 44.2) * mm, "end": v(-60, 38.83) * mm});
            skArc(sketch, "E79.16", {"start": v(54.26, 47.88) * mm, "mid": v(0, 60) * mm, "end": v(-54.26, 47.88) * mm});
            skArc(sketch, "E79.17", {"start": v(60, 38.83) * mm, "mid": v(58.44, 44.2) * mm, "end": v(54.26, 47.88) * mm});
            skLineSegment(sketch, "E79.18", {"start": v(60, 38.83) * mm, "end": v(60, -38.83) * mm});
            skArc(sketch, "E79.19", {"start": v(54.26, -47.88) * mm, "mid": v(58.44, -44.2) * mm, "end": v(60, -38.83) * mm});
            skPoint(sketch, "E80.endSnap0", {"position": v(0, 74.25) * mm});
            skLineSegment(sketch, "E81", {"start": v(0, 74.25) * mm, "end": v(0, 104.25) * mm, "construction": true});
            skCircle(sketch, "E82", {"center": v(0, 104.25) * mm, "radius": 6 * mm});
            skLineSegment(sketch, "E83", {"start": v(-33, 74.25) * mm, "end": v(-15, 92.25) * mm});
            skLineSegment(sketch, "E84", {"start": v(-15, 92.25) * mm, "end": v(-15, 104.25) * mm});
            skLineSegment(sketch, "E85", {"start": v(15, 104.25) * mm, "end": v(15, 92.25) * mm});
            skLineSegment(sketch, "E86", {"start": v(15, 92.25) * mm, "end": v(33, 74.25) * mm});
            skArc(sketch, "E87", {"start": v(15, 104.25) * mm, "mid": v(0, 119.25) * mm, "end": v(-15, 104.25) * mm});
            skLineSegment(sketch, "E88", {"start": v(-74.25, 0) * mm, "end": v(74.25, 0) * mm, "construction": true});
            skArc(sketch, "E89.MirrorCS", {"start": v(15, -104.25) * mm, "mid": v(0, -119.25) * mm, "end": v(-15, -104.25) * mm});
            skLineSegment(sketch, "E90.MirrorCS", {"start": v(15, -104.25) * mm, "end": v(15, -92.25) * mm});
            skLineSegment(sketch, "E91.MirrorCS", {"start": v(-15, -92.25) * mm, "end": v(-15, -104.25) * mm});
            skCircle(sketch, "E92.MirrorC", {"center": v(0, -104.25) * mm, "radius": 6 * mm});
            skLineSegment(sketch, "E93.MirrorCS", {"start": v(15, -92.25) * mm, "end": v(33, -74.25) * mm});
            skLineSegment(sketch, "E94.MirrorCS", {"start": v(-33, -74.25) * mm, "end": v(-15, -92.25) * mm});
            skLineSegment(sketch, "E95.MirrorCS", {"start": v(0, -74.25) * mm, "end": v(0, -104.25) * mm, "construction": true});
            skPoint(sketch, "E96.MirrorP", {"position": v(0, -74.25) * mm});
            skSolve(sketch);
        }
        {
            var Q0;
            Q0=makeQuery(id+"F16.imprint","IMPRINT",FACE,{"disambiguationData":[TD([[makeQuery(id+"F16.imprint","IMPRINT",EDGE,{"derivedFrom":sQuery(id+"F16.wireOp",EDGE,"E82")}),-1.0]])]});
            var Q1;
            Q1=makeQuery(id+"F16.imprint","IMPRINT",FACE,{"disambiguationData":[TD([[makeQuery(id+"F16.imprint","IMPRINT",EDGE,{"derivedFrom":sQuery(id+"F16.wireOp",EDGE,"E89.MirrorCS")}),-1.0]])]});
            var Q2;
            Q2=makeQuery(id+"F16.imprint","IMPRINT",FACE,{"disambiguationData":[TD([[makeQuery(id+"F16.imprint","IMPRINT",EDGE,{"derivedFrom":sQuery(id+"F16.wireOp",EDGE,"E79.0")}),-1.0]])]});
            var Q3;
            Q3=makeQuery(id+"F2.opExtrude","CAP_FACE",FACE,{"disambiguationData":[OSD([sQuery(id+"F0.wireOp",EDGE,"E12"),sQuery(id+"F0.wireOp",EDGE,"E13"),sQuery(id+"F0.wireOp",EDGE,"E14"),sQuery(id+"F0.wireOp",EDGE,"E15"),sQuery(id+"F0.wireOp",EDGE,"E17.filletArc"),sQuery(id+"F0.wireOp",EDGE,"E18.filletArc"),sQuery(id+"F0.wireOp",EDGE,"E19.filletArc"),sQuery(id+"F0.wireOp",EDGE,"E20.filletArc"),sQuery(id+"F0.wireOp",EDGE,"E25.0"),sQuery(id+"F0.wireOp",EDGE,"E25.1"),sQuery(id+"F0.wireOp",EDGE,"E25.2"),sQuery(id+"F0.wireOp",EDGE,"E25.3"),sQuery(id+"F0.wireOp",EDGE,"E25.4"),sQuery(id+"F0.wireOp",EDGE,"E25.5"),sQuery(id+"F0.wireOp",EDGE,"E25.6"),sQuery(id+"F0.wireOp",EDGE,"E25.7")])],"isStart":false});
            extrude(context, id + "F17", {"entities" : qUnion([Q0, Q1, Q2]), "endBound" : BoundingType.UP_TO_SURFACE, "endBoundEntityFace" : qUnion([Q3]), "depth" : 25 * mm});
        }
    });
